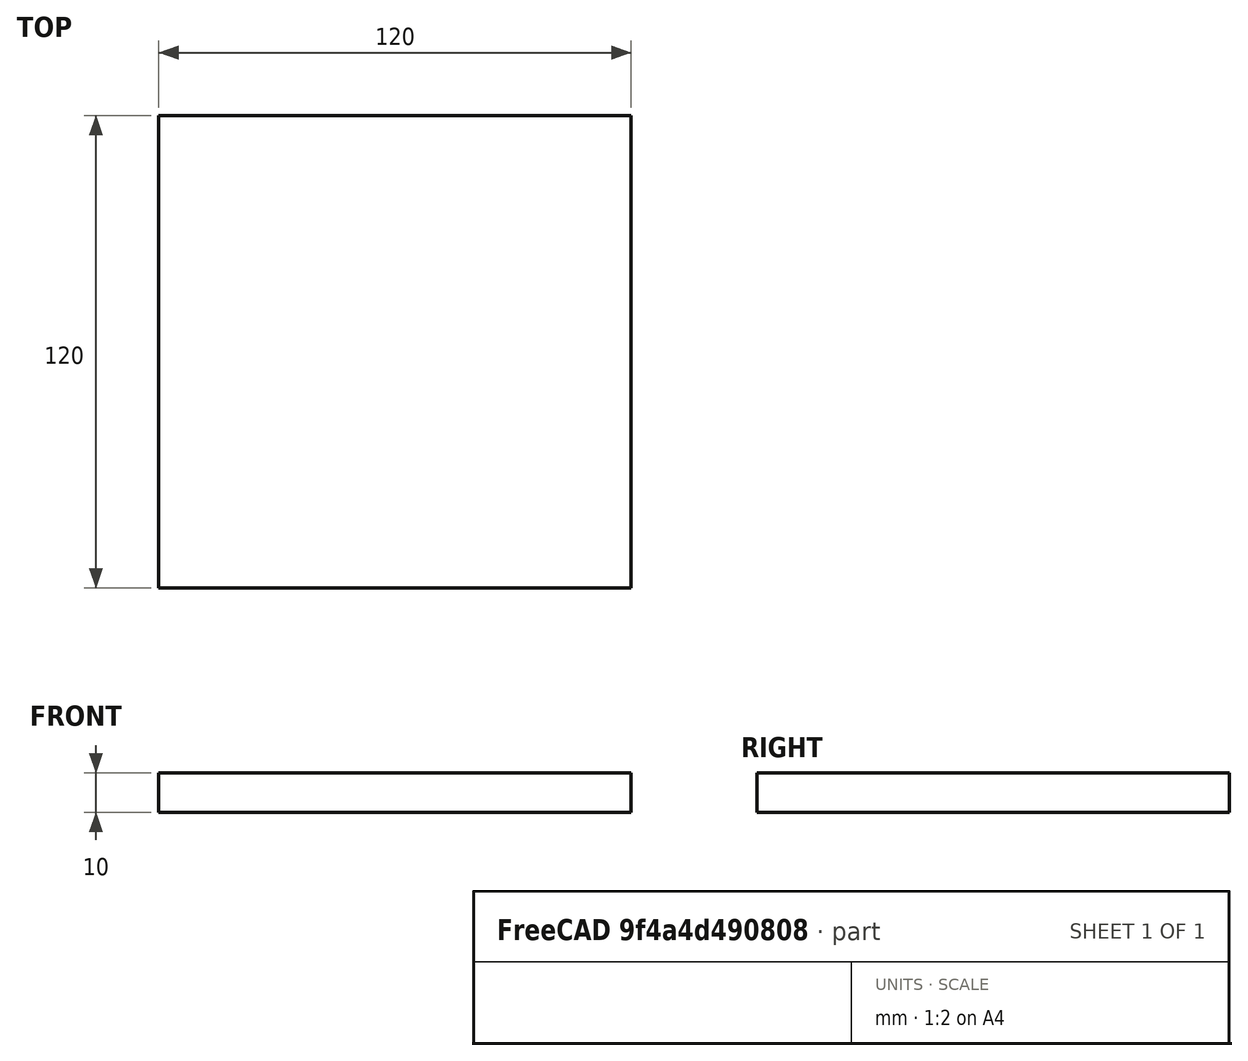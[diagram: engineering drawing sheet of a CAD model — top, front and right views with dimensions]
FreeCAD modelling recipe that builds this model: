
FCSTD DOCUMENT  (FreeCAD 0.16R6703 (Git))
Label: box_topbottom
License: All rights reserved
LicenseURL: http://en.wikipedia.org/wiki/All_rights_reserved
objects: Sketcher::SketchObject×1, PartDesign::Pad×1
note: 3 computed .brp shape members not serialized (recipe doc carries the construction recipe); baked Part::Feature solids carry a one-line shape summary decoded from their .brp

FEATURE [Sketcher::SketchObject] Sketch
  sketch-geometry (4):
    g0: LineSegment StartX=0 StartY=0 StartZ=0 EndX=120 EndY=0 EndZ=0
    g1: LineSegment StartX=120 StartY=0 StartZ=0 EndX=120 EndY=120 EndZ=0
    g2: LineSegment StartX=120 StartY=120 StartZ=0 EndX=0 EndY=120 EndZ=0
    g3: LineSegment StartX=0 StartY=120 StartZ=0 EndX=0 EndY=0 EndZ=0
  constraints (11):
    c: Coincident(g0,g1)
    c: Coincident(g1,g2)
    c: Coincident(g2,g3)
    c: Coincident(g3,g0)
    c: Horizontal(g0)
    c: Horizontal(g2)
    c: Vertical(g1)
    c: Vertical(g3)
    c: Coincident(g0,g-1)
    c: Distance(g2) = 120
    c: Distance(g3) = 120
FEATURE [PartDesign::Pad] Pad
  Length = 10
  Length2 = 100
  Sketch = -> Sketch
  Type = 0
